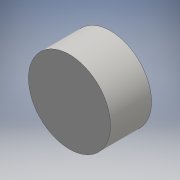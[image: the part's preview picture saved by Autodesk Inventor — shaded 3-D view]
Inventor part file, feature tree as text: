
AUTODESK INVENTOR PART (.ipt)
format: ipt  version: 2016 (Build 200138000, 138)  size: 97,280 bytes
history: native  units: mm
features: sketch x2, extrude x1
ambient origin geometry x8: Origin, YZ Plane, XZ Plane, XY Plane, X Axis, Y Axis, Z Axis, Center Point
bodies: Solid1 (feature_tree)
feature tree (3):
  extrude  "Extrusion1"  Depth=10.0mm TaperAngle=0.0deg
  sketch  "Sketch2"  dims[d3=6.981317mm d4=5.0mm d5=8.0mm]
  sketch  "Sketch1"  dims[d0=20.0mm d1=10.0mm d2=0.0mm]
